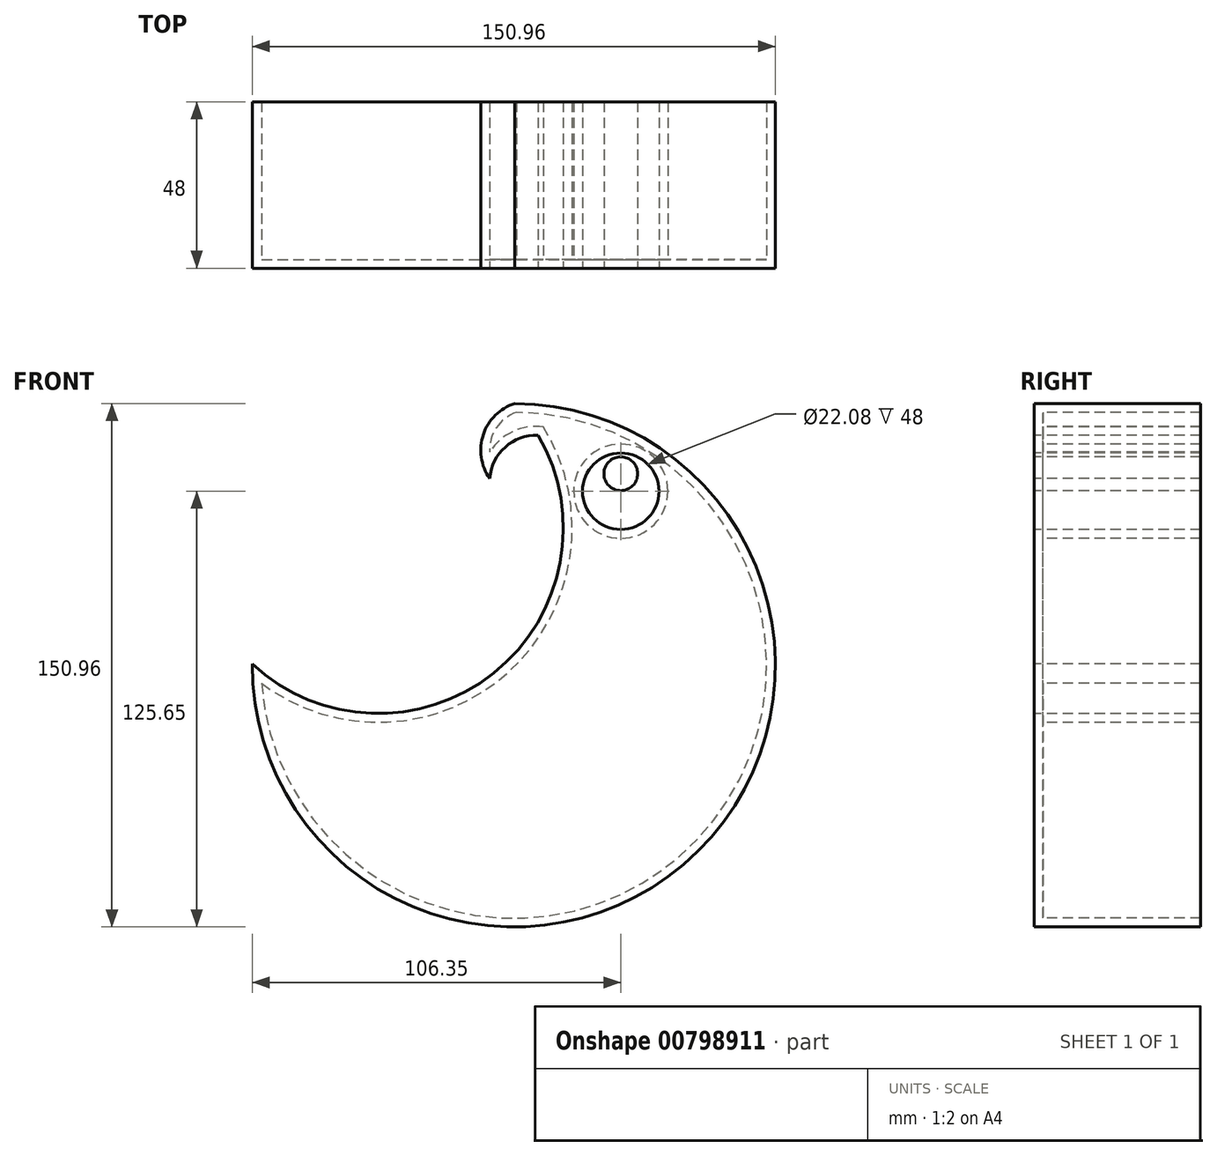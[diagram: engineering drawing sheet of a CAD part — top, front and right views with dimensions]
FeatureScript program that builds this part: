
annotation { "Feature Type Name" : "Feature", "Feature Type Description" : "" }
export const myFeature = defineFeature(function(context is Context, id is Id, definition is map)
    precondition{}
    {
        {
            var Q0;
            Q0=qCreatedBy(makeId("Front.planeOp"),FACE);
            var sketch = newSketch(context, id + "F0", { "sketchPlane" : qUnion([Q0])});
            skArc(sketch, "E0", {"start": v(-75.8, 0) * mm, "mid": v(52.82, -53.98) * mm, "end": v(0, 75.11) * mm});
            skArc(sketch, "E1", {"start": v(-75.8, 0) * mm, "mid": v(-1.84, 1.17) * mm, "end": v(0, 75.11) * mm});
            skArc(sketch, "E2", {"start": v(0, 75.11) * mm, "mid": v(-9.12, 66.15) * mm, "end": v(-7.26, 53.5) * mm});
            skArc(sketch, "E3", {"start": v(6.74, 65.94) * mm, "mid": v(-2.77, 62.55) * mm, "end": v(-7.26, 53.5) * mm});
            skCircle(sketch, "E4", {"center": v(30.55, 49.8) * mm, "radius": 11.04 * mm});
            skCircle(sketch, "E5", {"center": v(30.55, 54.86) * mm, "radius": 4.87 * mm});
            skCircle(sketch, "E6", {"center": v(30.55, 54.86) * mm, "radius": 2.14 * mm});
            skArc(sketch, "E7", {"start": v(12.12, 53.03) * mm, "mid": v(3.16, 51.77) * mm, "end": v(-3.88, 46.08) * mm});
            skArc(sketch, "E8", {"start": v(13.89, 42.07) * mm, "mid": v(5.37, 45.7) * mm, "end": v(-3.88, 46.08) * mm});
            skArc(sketch, "E9", {"start": v(-66, 17.38) * mm, "mid": v(-72.39, 9.53) * mm, "end": v(-75.8, 0) * mm});
            skArc(sketch, "E10", {"start": v(-66, 17.38) * mm, "mid": v(-66.68, 4.25) * mm, "end": v(-63.58, -8.52) * mm});
            skArc(sketch, "E11", {"start": v(-46.76, 11.3) * mm, "mid": v(-54.43, 0.87) * mm, "end": v(-54.64, -12.08) * mm});
            skArc(sketch, "E12", {"start": v(-46.76, 11.3) * mm, "mid": v(-46.64, -2.02) * mm, "end": v(-41.36, -14.26) * mm});
            skArc(sketch, "E13", {"start": v(12.12, 25.17) * mm, "mid": v(4.36, 34.8) * mm, "end": v(-7.93, 36.17) * mm});
            skArc(sketch, "E14", {"start": v(6.17, 11.3) * mm, "mid": v(3.54, 26.25) * mm, "end": v(-7.93, 36.17) * mm});
            skArc(sketch, "E15", {"start": v(-34.21, 11.3) * mm, "mid": v(-38.22, -1.37) * mm, "end": v(-34.21, -14.04) * mm});
            skArc(sketch, "E16", {"start": v(-34.21, 11.3) * mm, "mid": v(-31.68, -2.05) * mm, "end": v(-21.7, -11.27) * mm});
            skSolve(sketch);
        }
        {
            var Q0;
            Q0 = qSketchRegion(id + "F0", true);
            var Q1;
            Q1=makeQuery(id+"F0.imprint","IMPRINT",FACE,{"disambiguationData":[TD([[makeQuery(id+"F0.imprint","IMPRINT",EDGE,{"derivedFrom":sQuery(id+"F0.wireOp",EDGE,"E6")}),1.0]])]});
            var Q2;
            Q2=makeQuery(id+"F0.imprint","IMPRINT",FACE,{"disambiguationData":[TD([[makeQuery(id+"F0.imprint","IMPRINT",EDGE,{"derivedFrom":sQuery(id+"F0.wireOp",EDGE,"E5")}),1.0]])]});
            extrude(context, id + "F1", {"entities" : qUnion([Q0, Q1, Q2]), "oppositeDirection" : true, "depth" : 48 * mm, "offsetDistance" : 25.4 * mm});
        }
        {
            var Q0;
            Q0=makeQuery(id+"F1.opExtrude","CAP_FACE",FACE,{"disambiguationData":[OSD([sQuery(id+"F0.wireOp",EDGE,"E5")])],"isStart":false});
            extrude(context, id + "F2", {"entities" : qUnion([Q0]), "operationType" : NewBodyOperationType.ADD, "oppositeDirection" : true, "depth" : 3.8 * mm, "offsetDistance" : 25.4 * mm});
        }
        {
            var Q0;
            Q0=makeQuery(id+"F1.opExtrude","CAP_FACE",FACE,{"disambiguationData":[OSD([sQuery(id+"F0.wireOp",EDGE,"E0"),sQuery(id+"F0.wireOp",EDGE,"E1"),sQuery(id+"F0.wireOp",EDGE,"E2"),sQuery(id+"F0.wireOp",EDGE,"E3"),sQuery(id+"F0.wireOp",EDGE,"E4"),sQuery(id+"F0.wireOp",EDGE,"E7"),sQuery(id+"F0.wireOp",EDGE,"E8"),sQuery(id+"F0.wireOp",EDGE,"E9"),sQuery(id+"F0.wireOp",EDGE,"E10"),sQuery(id+"F0.wireOp",EDGE,"E11"),sQuery(id+"F0.wireOp",EDGE,"E12"),sQuery(id+"F0.wireOp",EDGE,"E13"),sQuery(id+"F0.wireOp",EDGE,"E14"),sQuery(id+"F0.wireOp",EDGE,"E15"),sQuery(id+"F0.wireOp",EDGE,"E16")])],"isStart":false});
            shell(context, id + "F3", {"entities" : qUnion([Q0]), "thickness" : 2.54 * mm});
        }
    });
